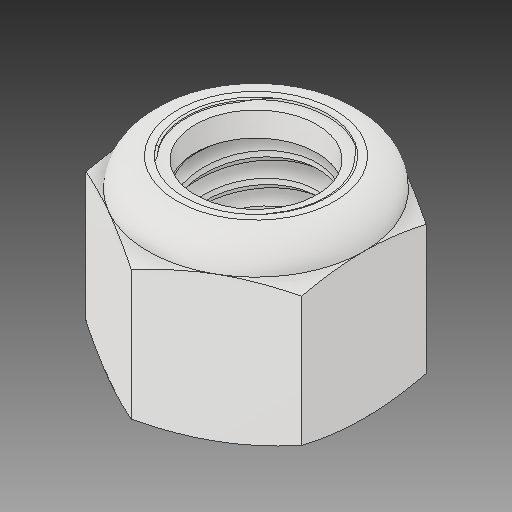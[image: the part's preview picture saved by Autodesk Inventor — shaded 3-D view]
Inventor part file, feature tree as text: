
AUTODESK INVENTOR PART (.ipt)
format: ipt  version: 2019 (Build 230136000, 136)  size: 337,920 bytes
history: native  units: in
note: dims shown in document units (in); Inventor stores cm internally (conversion verified against a paired STEP export)
features: other x1, revolve x1
ambient origin geometry x8: Origin, YZ Plane, XZ Plane, XY Plane, X Axis, Y Axis, Z Axis, Center Point
bodies: Solid1 (feature_tree), Solid2 (feature_tree)
feature tree (2):
  other  "Cut-Revolve4"
  revolve  "Revolve2"  [1 undecoded]
note: 1 required parameter value undecoded (feature->parameter linkage not recoverable at this tier; creation-order binding heuristic only, values carry confidence <= 0.55)
